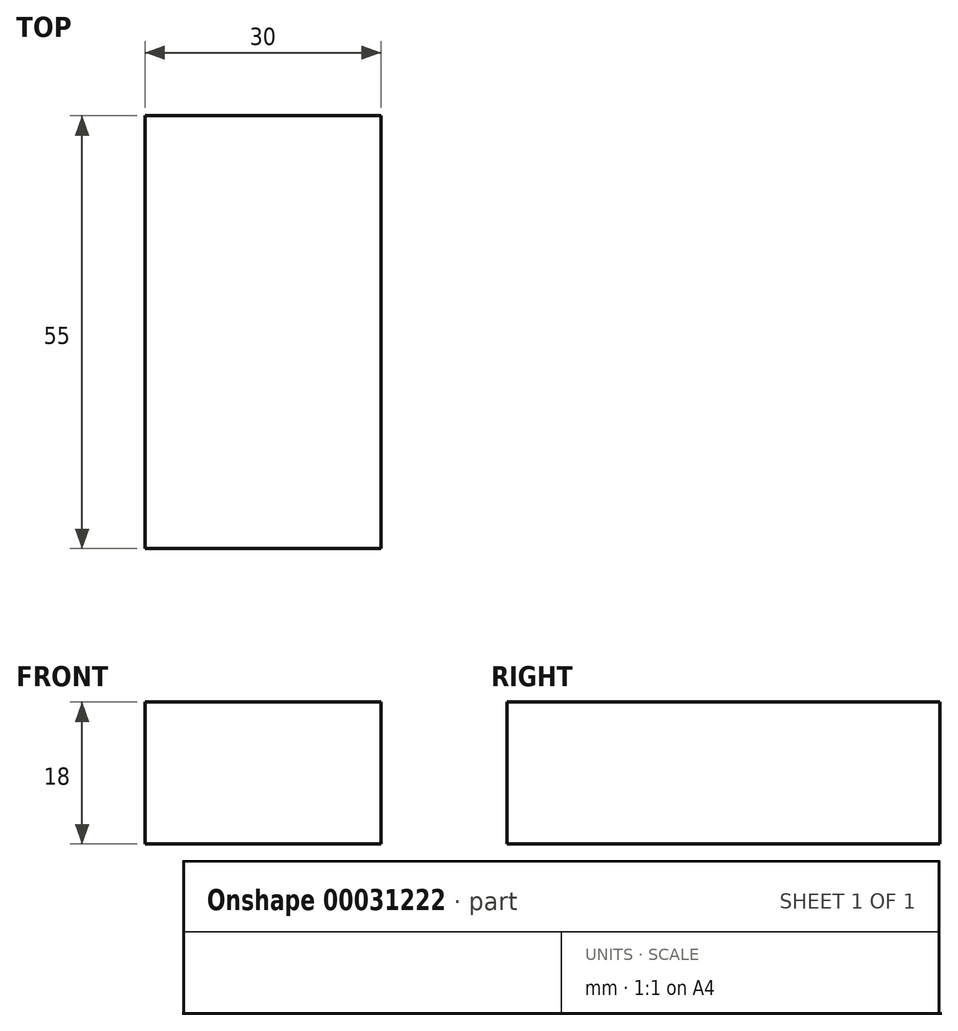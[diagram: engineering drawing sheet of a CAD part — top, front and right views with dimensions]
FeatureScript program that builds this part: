
annotation { "Feature Type Name" : "Feature", "Feature Type Description" : "" }
export const myFeature = defineFeature(function(context is Context, id is Id, definition is map)
    precondition{}
    {
        {
            var Q0;
            Q0=qCreatedBy(makeId("Top.planeOp"),FACE);
            var sketch = newSketch(context, id + "F0", { "sketchPlane" : qUnion([Q0])});
            skLineSegment(sketch, "E0.bottom", {"start": v(15, -27.5) * mm, "end": v(-15, -27.5) * mm});
            skLineSegment(sketch, "E0.top", {"start": v(15, 27.5) * mm, "end": v(-15, 27.5) * mm});
            skLineSegment(sketch, "E0.left", {"start": v(15, -27.5) * mm, "end": v(15, 27.5) * mm});
            skLineSegment(sketch, "E0.right", {"start": v(-15, -27.5) * mm, "end": v(-15, 27.5) * mm});
            skPoint(sketch, "E0.middle", {"position": v(0, 0) * mm});
            skSolve(sketch);
        }
        {
            var Q0;
            Q0 = qSketchRegion(id + "F0", true);
            extrude(context, id + "F1", {"entities" : qUnion([Q0]), "depth" : 18 * mm});
        }
    });
